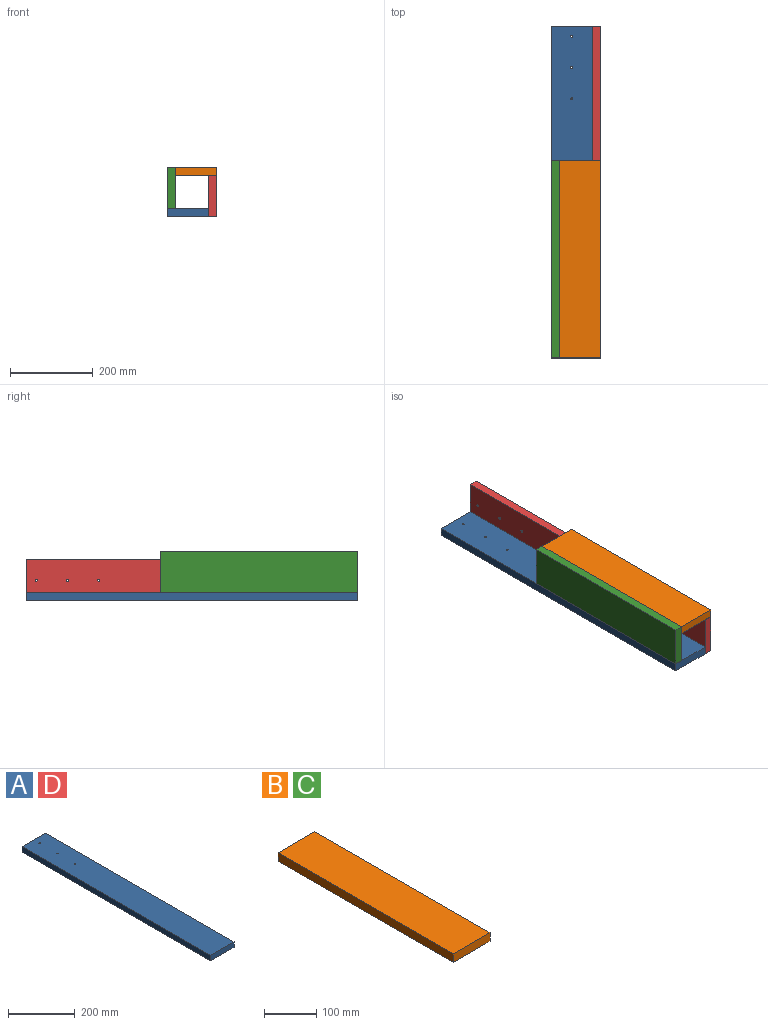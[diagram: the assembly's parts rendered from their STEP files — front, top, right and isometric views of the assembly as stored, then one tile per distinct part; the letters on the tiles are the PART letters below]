
ASSEMBLY  parts=4 mates=12
PART A: 9 faces, bbox 100x800x20 mm
  f0: plane 800x20mm, normal (-1,0,0), area 16000mm2, adj f1,f3,f4,f5
  f1: plane 100x20mm, normal (0,-1,0), area 2000mm2, adj f0,f2,f4,f5
  f2: plane 800x20mm, normal (1,0,0), area 16000mm2, adj f1,f3,f4,f5
  f3: plane 100x20mm, normal (0,1,0), area 2000mm2, adj f0,f2,f4,f5
  f4: plane 800x100mm, normal (0,0,1), area 79941.1mm2, adj f0,f1,f2,f3,f6,f7,f8
  f5: plane 800x100mm, normal (0,0,-1), area 79941.1mm2, adj f0,f1,f2,f3,f6,f7,f8
  f6: cylinder r=2.5mm len=20mm, axis (0,0,1), area 314.2mm2, adj f4,f5
  f7: cylinder r=2.5mm len=20mm, axis (0,0,1), area 314.2mm2, adj f4,f5
  f8: cylinder r=2.5mm len=20mm, axis (0,0,1), area 314.2mm2, adj f4,f5
PART B: 6 faces, bbox 100x476x20 mm
  f0: plane 476x20mm, normal (-1,0,0), area 9520mm2, adj f1,f3,f4,f5
  f1: plane 100x20mm, normal (0,-1,0), area 2000mm2, adj f0,f2,f4,f5
  f2: plane 476x20mm, normal (1,0,0), area 9520mm2, adj f1,f3,f4,f5
  f3: plane 100x20mm, normal (0,1,0), area 2000mm2, adj f0,f2,f4,f5
  f4: plane 476x100mm, normal (0,0,1), area 47600mm2, adj f0,f1,f2,f3
  f5: plane 476x100mm, normal (0,0,-1), area 47600mm2, adj f0,f1,f2,f3
PART C: same geometry as B
PART D: same geometry as A
PLACE A t=(489.81,-357.85,179.11)mm
PLACE B t=(509.81,-357.85,279.11)mm
PLACE C rot(axis=(0,-1,0),90deg) t=(509.81,-357.85,199.11)mm
PLACE D rot(axis=(0,-1,0),90deg) t=(609.81,-357.85,179.11)mm
MATE parallel A.f3 <-> D.f3  axis (0,1,0) through (489.81,442.15,199.11)mm
MATE parallel C.f1 <-> A.f1  axis (0,-1,0) through (499.81,-357.85,249.11)mm
MATE parallel A.f1 <-> D.f1  axis (0,-1,0) through (539.81,-357.85,189.11)mm
MATE parallel A.f5 <-> D.f0  axis (0,0,-1) through (539.81,41.93,179.11)mm
MATE planar A.f2 <-> D.f4  axis (1,0,0) through (589.81,42.15,189.11)mm
MATE parallel A.f4 <-> D.f2  axis (0,0,1) through (489.81,42.15,199.11)mm
MATE parallel A.f5 <-> D.f0  axis (0,0,-1) through (539.81,41.93,179.11)mm
MATE parallel C.f4 <-> A.f0  axis (-1,0,0) through (489.81,-119.85,249.11)mm
MATE parallel A.f5 <-> D.f0  axis (0,0,-1) through (539.81,41.93,179.11)mm
MATE planar C.f5 <-> B.f0  axis (1,0,0) through (509.81,-119.85,249.11)mm
MATE planar A.f4 <-> C.f0  axis (0,0,1) through (539.81,41.93,199.11)mm
MATE parallel C.f3 <-> A.f3  axis (0,1,0) through (499.81,118.15,249.11)mm
